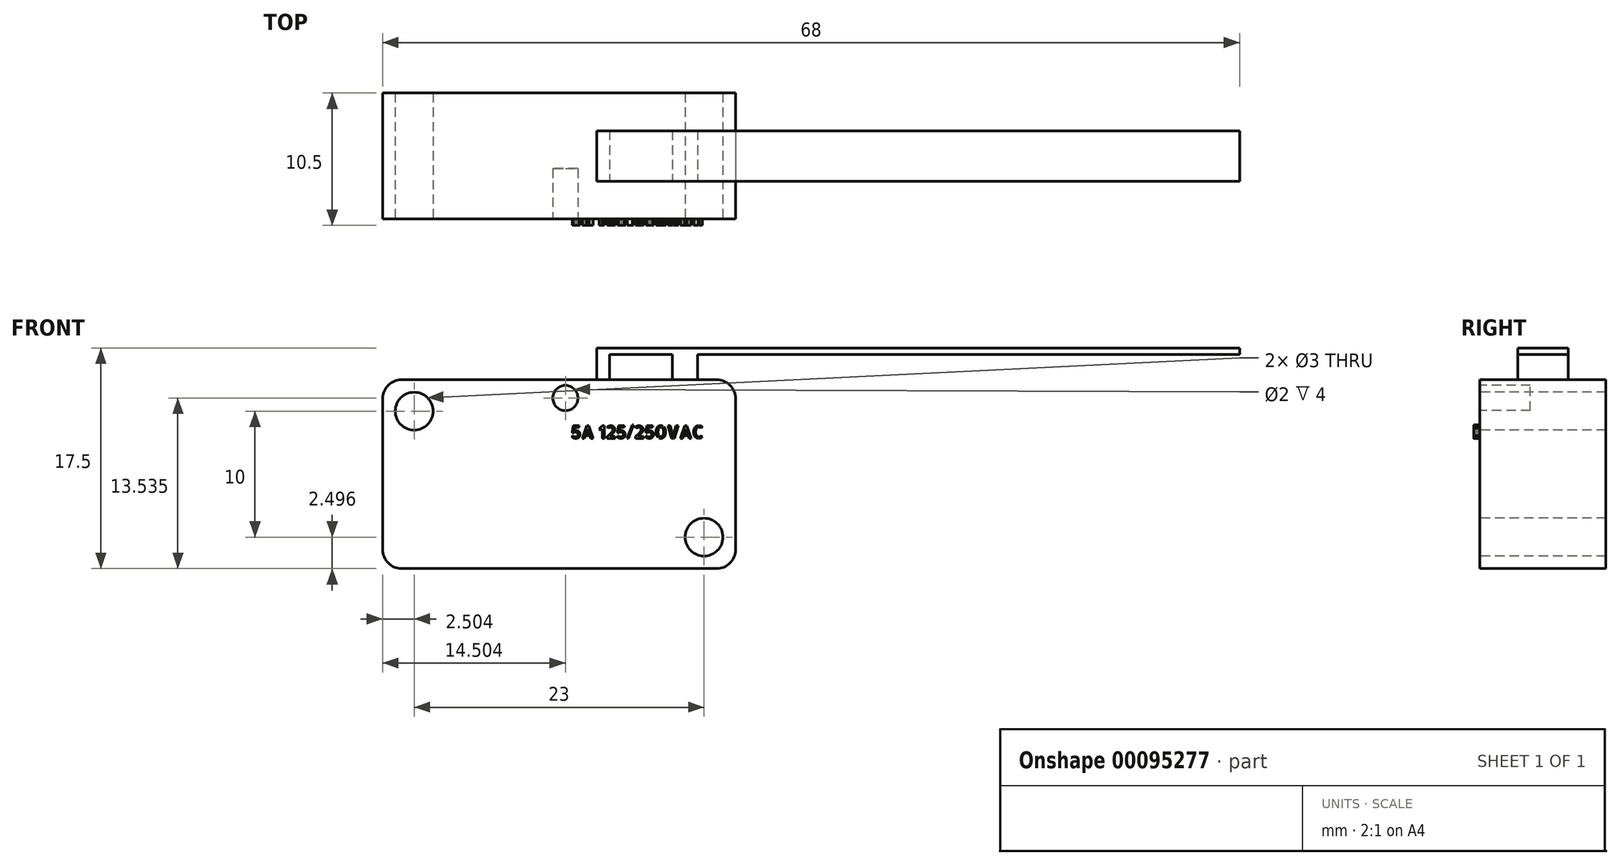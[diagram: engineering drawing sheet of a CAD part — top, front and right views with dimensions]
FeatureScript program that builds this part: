
annotation { "Feature Type Name" : "Feature", "Feature Type Description" : "" }
export const myFeature = defineFeature(function(context is Context, id is Id, definition is map)
    precondition{}
    {
        {
            var Q0;
            Q0=qCreatedBy(makeId("Front.planeOp"),FACE);
            var sketch = newSketch(context, id + "F0", { "sketchPlane" : qUnion([Q0])});
            skLineSegment(sketch, "E0.bottom", {"start": v(-13.65, 9.2) * mm, "end": v(14.35, 9.2) * mm});
            skLineSegment(sketch, "E0.top", {"start": v(-13.65, -5.8) * mm, "end": v(14.35, -5.8) * mm});
            skLineSegment(sketch, "E0.left", {"start": v(-13.65, 9.2) * mm, "end": v(-13.65, -5.8) * mm});
            skLineSegment(sketch, "E0.right", {"start": v(14.35, 9.2) * mm, "end": v(14.35, -5.8) * mm});
            skCircle(sketch, "E1", {"center": v(11.85, -3.3) * mm, "radius": 1.5 * mm});
            skCircle(sketch, "E2", {"center": v(-11.15, 6.7) * mm, "radius": 1.5 * mm});
            skCircle(sketch, "E3", {"center": v(-12.15, 7.7) * mm, "radius": 1.5 * mm});
            skCircle(sketch, "E4", {"center": v(12.85, -4.3) * mm, "radius": 1.5 * mm});
            skCircle(sketch, "E5", {"center": v(12.85, 7.7) * mm, "radius": 1.5 * mm});
            skCircle(sketch, "E6", {"center": v(-12.15, -4.3) * mm, "radius": 1.5 * mm});
            skCircle(sketch, "E7", {"center": v(0.85, 7.74) * mm, "radius": 1 * mm});
            skSolve(sketch);
        }
        {
            var Q0;
            {var subQ0=sQuery(id+"F0.wireOp",EDGE,"E4");var subQ1=sQuery(id+"F0.wireOp",EDGE,"E1");var subQ2=makeQuery(id+"F0.imprint","INTERSECT",VERTEX,{"disambiguationData":[OD(0.0)],"derivedFrom":[subQ1,subQ0]});Q0=makeQuery(id+"F0.imprint","IMPRINT",FACE,{"disambiguationData":[TD([[makeQuery(id+"F0.imprint","IMPRINT",EDGE,{"disambiguationData":[TD([[subQ2,1.0]])],"derivedFrom":subQ1}),-1.0]])]});}
            var Q1;
            Q1=makeQuery(id+"F0.imprint","IMPRINT",FACE,{"disambiguationData":[TD([[makeQuery(id+"F0.imprint","IMPRINT",EDGE,{"derivedFrom":sQuery(id+"F0.wireOp",EDGE,"E7")}),-1.0]])]});
            var Q2;
            {var subQ0=sQuery(id+"F0.wireOp",EDGE,"E3");var subQ1=sQuery(id+"F0.wireOp",EDGE,"E2");var subQ2=makeQuery(id+"F0.imprint","INTERSECT",VERTEX,{"disambiguationData":[OD(0.0)],"derivedFrom":[subQ1,subQ0]});Q2=makeQuery(id+"F0.imprint","IMPRINT",FACE,{"disambiguationData":[TD([[makeQuery(id+"F0.imprint","IMPRINT",EDGE,{"disambiguationData":[TD([[subQ2,-1.0]])],"derivedFrom":subQ1}),-1.0]])]});}
            var Q3;
            {var subQ0=sQuery(id+"F0.wireOp",EDGE,"E6");var subQ1=makeQuery(id+"F0.imprint","INTERSECT",VERTEX,{"derivedFrom":[sQuery(id+"F0.wireOp",EDGE,"E0.top"),subQ0]});Q3=makeQuery(id+"F0.imprint","IMPRINT",FACE,{"disambiguationData":[TD([[makeQuery(id+"F0.imprint","IMPRINT",EDGE,{"disambiguationData":[TD([[subQ1,1.0]])],"derivedFrom":subQ0}),1.0]])]});}
            var Q4;
            {var subQ0=sQuery(id+"F0.wireOp",EDGE,"E5");var subQ1=makeQuery(id+"F0.imprint","INTERSECT",VERTEX,{"derivedFrom":[sQuery(id+"F0.wireOp",EDGE,"E0.bottom"),subQ0]});Q4=makeQuery(id+"F0.imprint","IMPRINT",FACE,{"disambiguationData":[TD([[makeQuery(id+"F0.imprint","IMPRINT",EDGE,{"disambiguationData":[TD([[subQ1,1.0]])],"derivedFrom":subQ0}),1.0]])]});}
            var Q5;
            Q5=makeQuery(id+"F0.imprint","IMPRINT",FACE,{"disambiguationData":[TD([[makeQuery(id+"F0.imprint","IMPRINT",EDGE,{"derivedFrom":sQuery(id+"F0.wireOp",EDGE,"E7")}),1.0]])]});
            extrude(context, id + "F1", {"entities" : qUnion([Q0, Q1, Q2, Q3, Q4, Q5]), "oppositeDirection" : true, "depth" : 10 * mm});
        }
        {
            var Q0;
            Q0=makeQuery(id+"F0.imprint","IMPRINT",FACE,{"disambiguationData":[TD([[makeQuery(id+"F0.imprint","IMPRINT",EDGE,{"derivedFrom":sQuery(id+"F0.wireOp",EDGE,"E7")}),1.0]])]});
            var Q1;
            Q1=sQuery(id+"F0.wireOp",EDGE,"E7");
            extrude(context, id + "F2", {"entities" : qUnion([Q0]), "operationType" : NewBodyOperationType.REMOVE, "surfaceEntities" : qUnion([Q1]), "oppositeDirection" : true, "depth" : 4 * mm});
        }
        {
            var Q0;
            Q0=makeQuery(id+"F1.opExtrude","SWEPT_FACE",FACE,{"disambiguationData":[OSD([sQuery(id+"F0.wireOp",EDGE,"E0.bottom")])]});
            var sketch = newSketch(context, id + "F3", { "sketchPlane" : qUnion([Q0])});
            skLineSegment(sketch, "E8.bottom", {"start": v(9.35, 7) * mm, "end": v(11.35, 7) * mm});
            skLineSegment(sketch, "E8.top", {"start": v(9.35, 3) * mm, "end": v(11.35, 3) * mm});
            skLineSegment(sketch, "E8.left", {"start": v(9.35, 7) * mm, "end": v(9.35, 3) * mm});
            skLineSegment(sketch, "E8.right", {"start": v(11.35, 7) * mm, "end": v(11.35, 3) * mm});
            skLineSegment(sketch, "E9.bottom", {"start": v(3.35, 7) * mm, "end": v(4.35, 7) * mm});
            skLineSegment(sketch, "E9.top", {"start": v(3.35, 3) * mm, "end": v(4.35, 3) * mm});
            skLineSegment(sketch, "E9.left", {"start": v(3.35, 7) * mm, "end": v(3.35, 3) * mm});
            skLineSegment(sketch, "E9.right", {"start": v(4.35, 7) * mm, "end": v(4.35, 3) * mm});
            skSolve(sketch);
        }
        {
            var Q0;
            Q0=makeQuery(id+"F3.imprint","IMPRINT",FACE,{"disambiguationData":[TD([[makeQuery(id+"F3.imprint","IMPRINT",EDGE,{"derivedFrom":sQuery(id+"F3.wireOp",EDGE,"E8.bottom")}),-1.0]])]});
            extrude(context, id + "F4", {"entities" : qUnion([Q0]), "depth" : 2 * mm});
        }
        {
            var Q0;
            Q0=makeQuery(id+"F1.opExtrude","CAP_FACE",FACE,{"disambiguationData":[OSD([sQuery(id+"F0.wireOp",EDGE,"E0.bottom"),sQuery(id+"F0.wireOp",EDGE,"E0.top"),sQuery(id+"F0.wireOp",EDGE,"E0.left"),sQuery(id+"F0.wireOp",EDGE,"E0.right"),sQuery(id+"F0.wireOp",EDGE,"E1"),sQuery(id+"F0.wireOp",EDGE,"E2"),sQuery(id+"F0.wireOp",EDGE,"E3"),sQuery(id+"F0.wireOp",EDGE,"E4"),sQuery(id+"F0.wireOp",EDGE,"E5"),sQuery(id+"F0.wireOp",EDGE,"E6")])],"isStart":true});
            var sketch = newSketch(context, id + "F5", { "sketchPlane" : qUnion([Q0])});
            skText(sketch, "E10", { "text": "5A 125/250VAC", "fontName": "AllertaStencil-Regular.ttf"});
            const initialGuessF5  = {"E10": [0.0013, 0.00455, 1, 0, 0.00099]};
            skSetInitialGuess(sketch, initialGuessF5);
            skSolve(sketch);
        }
        {
            var Q0;
            Q0 = qSketchRegion(id + "F5", true);
            extrude(context, id + "F6", {"entities" : qUnion([Q0]), "depth" : .5 * mm});
        }
        {
            var Q0;
            Q0=makeQuery(id+"F3.imprint","IMPRINT",FACE,{"disambiguationData":[TD([[makeQuery(id+"F3.imprint","IMPRINT",EDGE,{"derivedFrom":sQuery(id+"F3.wireOp",EDGE,"E9.bottom")}),-1.0]])]});
            extrude(context, id + "F7", {"entities" : qUnion([Q0]), "depth" : 2 * mm});
        }
        {
            var Q0;
            Q0=makeQuery(id+"F7.opExtrude","CAP_FACE",FACE,{"disambiguationData":[OSD([sQuery(id+"F3.wireOp",EDGE,"E9.bottom"),sQuery(id+"F3.wireOp",EDGE,"E9.top"),sQuery(id+"F3.wireOp",EDGE,"E9.left"),sQuery(id+"F3.wireOp",EDGE,"E9.right")])],"isStart":false});
            var sketch = newSketch(context, id + "F8", { "sketchPlane" : qUnion([Q0])});
            skLineSegment(sketch, "E11.bottom", {"start": v(3.35, 7) * mm, "end": v(54.35, 7) * mm});
            skLineSegment(sketch, "E11.top", {"start": v(3.35, 3) * mm, "end": v(54.35, 3) * mm});
            skLineSegment(sketch, "E11.left", {"start": v(3.35, 7) * mm, "end": v(3.35, 3) * mm});
            skLineSegment(sketch, "E11.right", {"start": v(54.35, 7) * mm, "end": v(54.35, 3) * mm});
            skSolve(sketch);
        }
        {
            var Q0;
            {var subQ2=sQuery(id+"F8.wireOp",EDGE,"E11.right");Q0=makeQuery(id+"F8.imprint","IMPRINT",FACE,{"disambiguationData":[TD([[makeQuery(id+"F8.imprint","IMPRINT",EDGE,{"derivedFrom":subQ2}),-1.0]])]});}
            var Q1;
            {var subQ0=sQuery(id+"F8.wireOp",EDGE,"E11.left");Q1=makeQuery(id+"F8.imprint","IMPRINT",FACE,{"disambiguationData":[TD([[makeQuery(id+"F8.imprint","IMPRINT",EDGE,{"derivedFrom":subQ0}),1.0]])]});}
            extrude(context, id + "F9", {"entities" : qUnion([Q0, Q1]), "operationType" : NewBodyOperationType.ADD, "depth" : .5 * mm});
        }
    });
